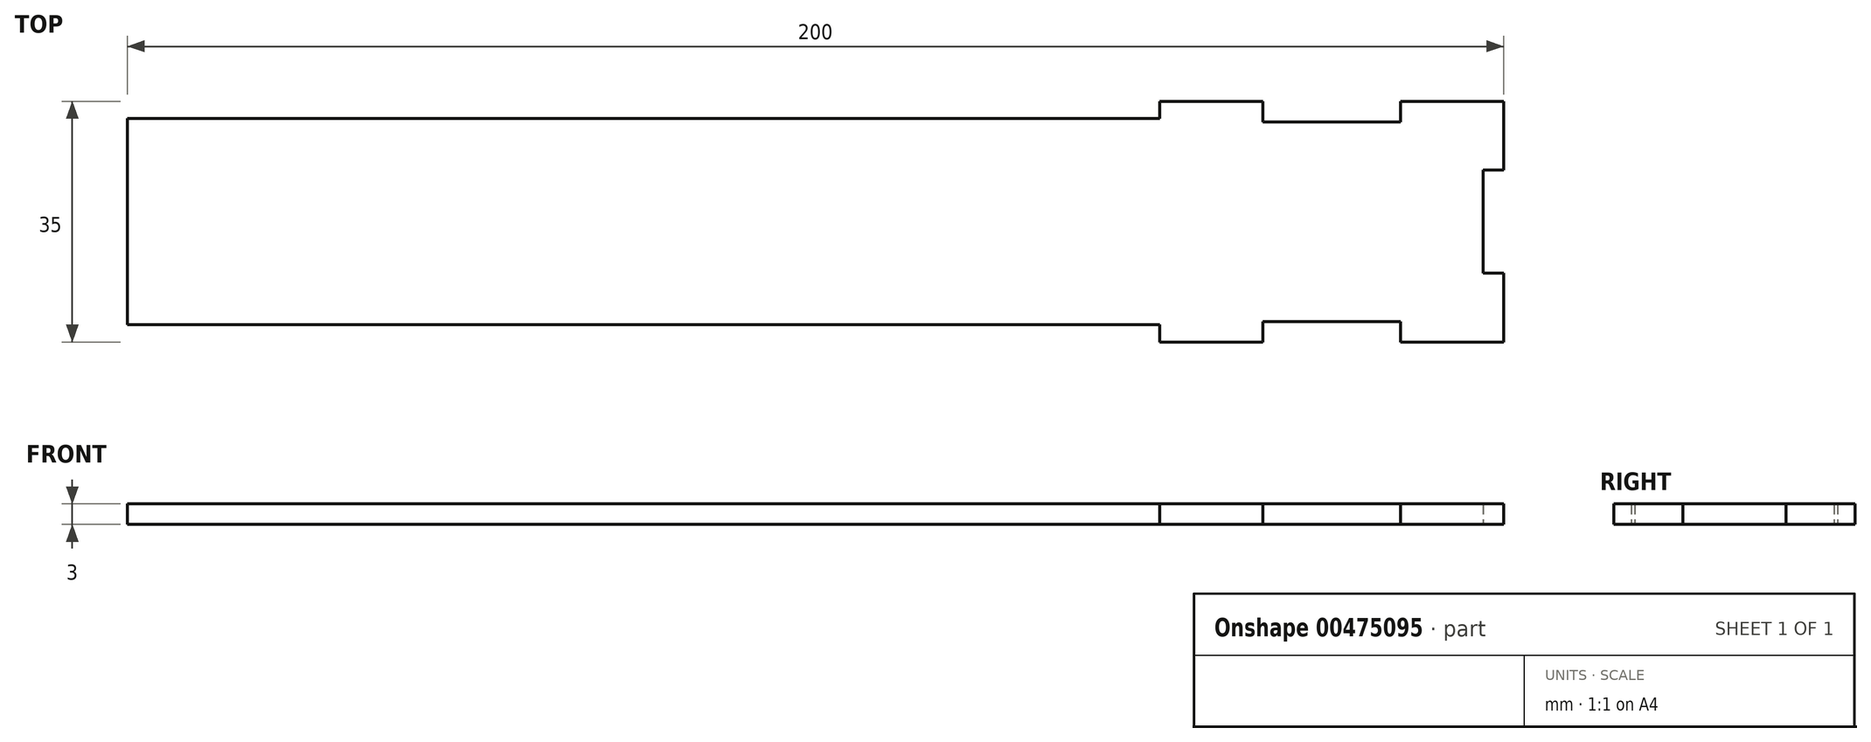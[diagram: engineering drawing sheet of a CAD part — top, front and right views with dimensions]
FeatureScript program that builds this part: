
annotation { "Feature Type Name" : "Feature", "Feature Type Description" : "" }
export const myFeature = defineFeature(function(context is Context, id is Id, definition is map)
    precondition{}
    {
        {
            var Q0;
            Q0=qCreatedBy(makeId("Top.planeOp"),FACE);
            var sketch = newSketch(context, id + "F0", { "sketchPlane" : qUnion([Q0])});
            skLineSegment(sketch, "E0", {"start": v(0, 0) * mm, "end": v(-150, 0) * mm});
            skLineSegment(sketch, "E1.left", {"start": v(0, 0) * mm, "end": v(0, 0) * mm});
            skLineSegment(sketch, "E1.right", {"start": v(-150, 0) * mm, "end": v(-150, 0) * mm});
            skLineSegment(sketch, "E2.bottom", {"start": v(-150, 18.52) * mm, "end": v(0, 18.52) * mm});
            skLineSegment(sketch, "E2.top", {"start": v(-150, 0) * mm, "end": v(0, 0) * mm});
            skLineSegment(sketch, "E2.left", {"start": v(-150, 18.52) * mm, "end": v(-150, 0) * mm});
            skLineSegment(sketch, "E2.right", {"start": v(0, 18.52) * mm, "end": v(0, 0) * mm});
            skLineSegment(sketch, "E3.bottom", {"start": v(-150, -11.48) * mm, "end": v(0, -11.48) * mm});
            skLineSegment(sketch, "E3.left", {"start": v(-150, -11.48) * mm, "end": v(-150, 0) * mm});
            skLineSegment(sketch, "E3.right", {"start": v(0, -11.48) * mm, "end": v(0, 0) * mm});
            skLineSegment(sketch, "E4", {"start": v(-150, 18.52) * mm, "end": v(-150, -11.48) * mm});
            skLineSegment(sketch, "E5", {"start": v(0, 18.52) * mm, "end": v(0, 21.02) * mm});
            skLineSegment(sketch, "E6", {"start": v(0, -11.48) * mm, "end": v(0, -13.98) * mm});
            skLineSegment(sketch, "E7", {"start": v(0, 21.02) * mm, "end": v(15, 21.02) * mm});
            skLineSegment(sketch, "E8", {"start": v(0, -13.98) * mm, "end": v(15, -13.98) * mm});
            skLineSegment(sketch, "E9", {"start": v(50, -13.98) * mm, "end": v(50, -3.98) * mm});
            skLineSegment(sketch, "E10", {"start": v(50, 21.02) * mm, "end": v(50, 11.02) * mm});
            skLineSegment(sketch, "E11", {"start": v(50, 11.02) * mm, "end": v(47, 11.02) * mm});
            skLineSegment(sketch, "E12", {"start": v(50, -3.98) * mm, "end": v(47, -3.98) * mm});
            skLineSegment(sketch, "E13", {"start": v(47, -3.98) * mm, "end": v(47, 11.02) * mm});
            skLineSegment(sketch, "E14.trimOffspring", {"start": v(50, 11.02) * mm, "end": v(50, 21.02) * mm});
            skLineSegment(sketch, "E15", {"start": v(50, 21.02) * mm, "end": v(35, 21.02) * mm});
            skLineSegment(sketch, "E16", {"start": v(15, 21.02) * mm, "end": v(15, 18.02) * mm});
            skLineSegment(sketch, "E17", {"start": v(15, 18.02) * mm, "end": v(35, 18.02) * mm});
            skLineSegment(sketch, "E18", {"start": v(35, 18.02) * mm, "end": v(35, 21.02) * mm});
            skLineSegment(sketch, "E19.trimOffspring", {"start": v(35, 21.02) * mm, "end": v(50, 21.02) * mm});
            skLineSegment(sketch, "E20", {"start": v(35, -13.98) * mm, "end": v(50, -13.98) * mm});
            skLineSegment(sketch, "E21", {"start": v(15, -13.98) * mm, "end": v(15, -10.98) * mm});
            skLineSegment(sketch, "E22", {"start": v(15, -10.98) * mm, "end": v(35, -10.98) * mm});
            skLineSegment(sketch, "E23", {"start": v(35, -10.98) * mm, "end": v(35, -13.98) * mm});
            skSolve(sketch);
        }
        {
            var Q0;
            {var subQ0=sQuery(id+"F0.wireOp",EDGE,"E2.bottom");Q0=makeQuery(id+"F0.imprint","IMPRINT",FACE,{"disambiguationData":[TD([[makeQuery(id+"F0.imprint","IMPRINT",EDGE,{"derivedFrom":subQ0}),-1.0]])]});}
            var Q1;
            {var subQ0=sQuery(id+"F0.wireOp",EDGE,"E3.bottom");Q1=makeQuery(id+"F0.imprint","IMPRINT",FACE,{"disambiguationData":[TD([[makeQuery(id+"F0.imprint","IMPRINT",EDGE,{"derivedFrom":subQ0}),1.0]])]});}
            var Q2;
            Q2=makeQuery(id+"F0.imprint","IMPRINT",FACE,{"disambiguationData":[TD([[makeQuery(id+"F0.imprint","IMPRINT",EDGE,{"derivedFrom":sQuery(id+"F0.wireOp",EDGE,"E2.right")}),1.0]])]});
            extrude(context, id + "F1", {"entities" : qUnion([Q0, Q1, Q2]), "depth" : 3 * mm});
        }
    });
